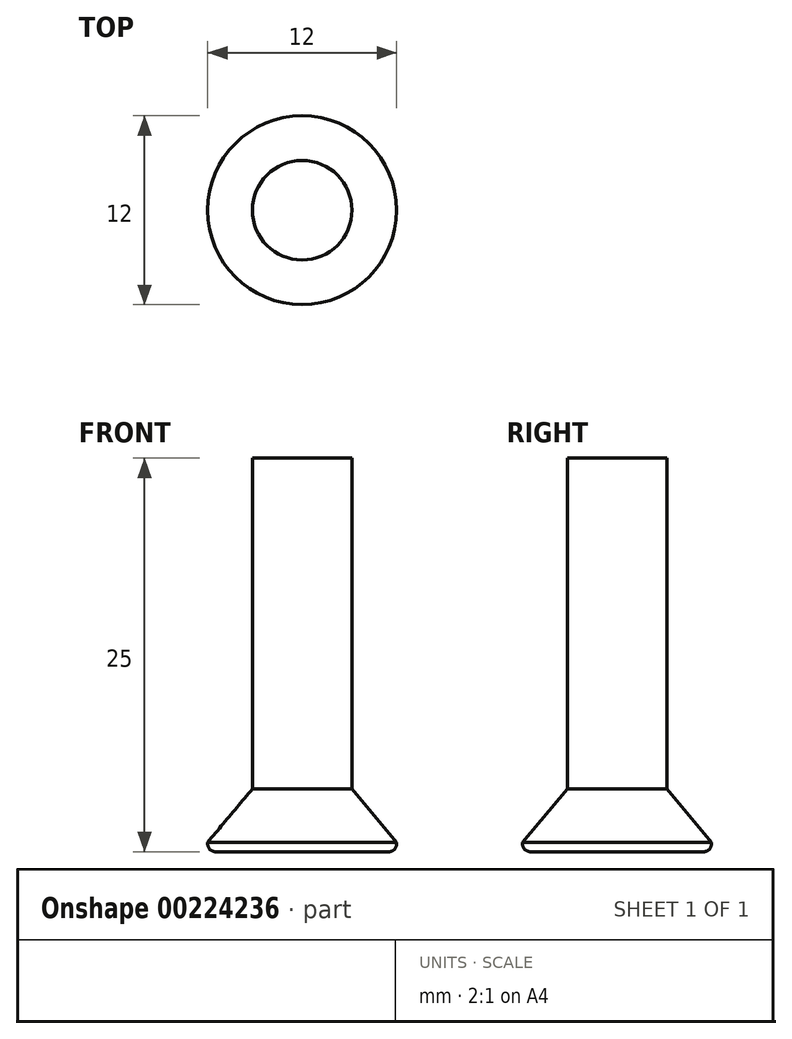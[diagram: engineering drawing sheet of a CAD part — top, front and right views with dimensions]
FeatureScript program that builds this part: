
annotation { "Feature Type Name" : "Feature", "Feature Type Description" : "" }
export const myFeature = defineFeature(function(context is Context, id is Id, definition is map)
    precondition{}
    {
        {
            var Q0;
            Q0=qCreatedBy(makeId("Top.planeOp"),FACE);
            var sketch = newSketch(context, id + "F0", { "sketchPlane" : qUnion([Q0])});
            skCircle(sketch, "E0", {"center": v(0, 0) * mm, "radius": 6 * mm});
            skCircle(sketch, "E1", {"center": v(0, 0) * mm, "radius": 3.16 * mm});
            skSolve(sketch);
        }
        {
            var Q0;
            Q0=makeQuery(id+"F0.imprint","IMPRINT",FACE,{"disambiguationData":[TD([[makeQuery(id+"F0.imprint","IMPRINT",EDGE,{"derivedFrom":sQuery(id+"F0.wireOp",EDGE,"E0")}),1.0]])]});
            extrude(context, id + "F1", {"entities" : qUnion([Q0]), "depth" : 4 * mm});
        }
        {
            var Q0;
            Q0=makeQuery(id+"F0.imprint","IMPRINT",FACE,{"disambiguationData":[TD([[makeQuery(id+"F0.imprint","IMPRINT",EDGE,{"derivedFrom":sQuery(id+"F0.wireOp",EDGE,"E1")}),1.0]])]});
            extrude(context, id + "F2", {"entities" : qUnion([Q0]), "operationType" : NewBodyOperationType.ADD, "depth" : 25 * mm});
        }
        {
            var Q0;
            Q0=makeQuery(id+"F1.opExtrude","CAP_EDGE",EDGE,{"disambiguationData":[OSD([sQuery(id+"F0.wireOp",EDGE,"E0")])],"isStart":false});
            chamfer(context, id + "F3", {"entities" : qUnion([Q0]), "chamferType" : ChamferType.OFFSET_ANGLE, "width" : 2.85 * mm, "oppositeDirection" : false, "angle" : 50 * degree, "tangentPropagation" : true});
        }
        {
            var Q0;
            Q0=makeQuery(id+"F1.opExtrude","CAP_EDGE",EDGE,{"disambiguationData":[OSD([sQuery(id+"F0.wireOp",EDGE,"E0")])],"isStart":true});
            fillet(context, id + "F4", {"entities" : qUnion([Q0]), "radius" : .5 * mm, "tangentPropagation" : true, "allowEdgeOverflow" : false});
        }
    });
